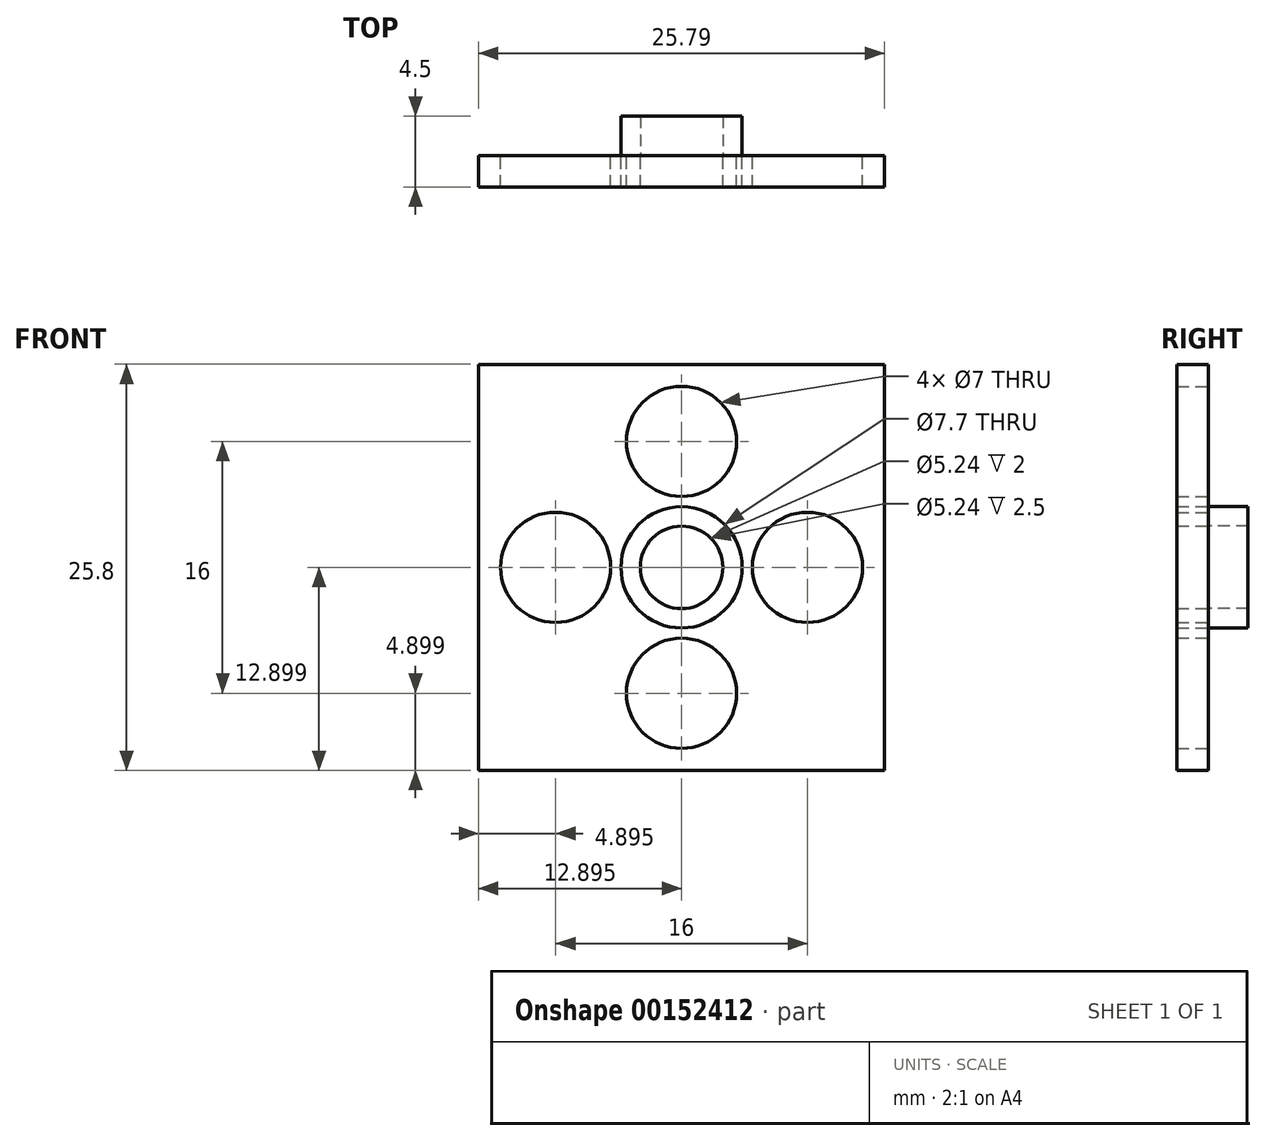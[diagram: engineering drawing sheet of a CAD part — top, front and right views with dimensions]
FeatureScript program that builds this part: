
annotation { "Feature Type Name" : "Feature", "Feature Type Description" : "" }
export const myFeature = defineFeature(function(context is Context, id is Id, definition is map)
    precondition{}
    {
        {
            var Q0;
            Q0=qCreatedBy(makeId("Front.planeOp"),FACE);
            var sketch = newSketch(context, id + "F0", { "sketchPlane" : qUnion([Q0])});
            skPoint(sketch, "E0.middle", {"position": v(0.36, -0.48) * mm});
            skLineSegment(sketch, "E1.top", {"start": v(-7.64, -8.48) * mm, "end": v(8.36, -8.48) * mm, "construction": true});
            skLineSegment(sketch, "E1.left", {"start": v(-7.64, 7.52) * mm, "end": v(-7.64, -8.48) * mm, "construction": true});
            skLineSegment(sketch, "E1.right", {"start": v(8.36, 7.52) * mm, "end": v(8.36, -8.48) * mm, "construction": true});
            skLineSegment(sketch, "E2", {"start": v(-7.64, 7.52) * mm, "end": v(8.36, 7.52) * mm, "construction": true});
            skLineSegment(sketch, "E3", {"start": v(0.36, -0.48) * mm, "end": v(-27.14, 27.02) * mm, "construction": true});
            skLineSegment(sketch, "E4", {"start": v(0.36, -0.48) * mm, "end": v(-27.14, -27.98) * mm, "construction": true});
            skLineSegment(sketch, "E5", {"start": v(0.36, -0.48) * mm, "end": v(27.86, 27.02) * mm, "construction": true});
            skLineSegment(sketch, "E6", {"start": v(0.36, -0.48) * mm, "end": v(27.86, -27.98) * mm, "construction": true});
            skLineSegment(sketch, "E7", {"start": v(0.36, -0.48) * mm, "end": v(0.36, 27.02) * mm, "construction": true});
            skLineSegment(sketch, "E8", {"start": v(0.36, -8.48) * mm, "end": v(0.36, -27.98) * mm, "construction": true});
            skPoint(sketch, "E9", {"position": v(-7.64, 7.52) * mm});
            skLineSegment(sketch, "E10", {"start": v(21.88, 21.04) * mm, "end": v(-21.17, 21.04) * mm, "construction": true});
            skLineSegment(sketch, "E11", {"start": v(-21.17, 21.04) * mm, "end": v(-21.17, -22) * mm, "construction": true});
            skLineSegment(sketch, "E12", {"start": v(-21.17, -22) * mm, "end": v(21.88, -22) * mm, "construction": true});
            skLineSegment(sketch, "E13", {"start": v(21.88, -22) * mm, "end": v(21.88, 21.04) * mm, "construction": true});
            skLineSegment(sketch, "E14", {"start": v(0.36, -0.48) * mm, "end": v(-19.04, -0.48) * mm, "construction": true});
            skLineSegment(sketch, "E15", {"start": v(-27.14, -0.48) * mm, "end": v(-19.04, -0.48) * mm, "construction": true});
            skLineSegment(sketch, "E16", {"start": v(0.36, -0.48) * mm, "end": v(27.86, -0.48) * mm, "construction": true});
            skLineSegment(sketch, "E17", {"start": v(0.36, -0.48) * mm, "end": v(0.36, -8.48) * mm, "construction": true});
            skCircle(sketch, "E18", {"center": v(8.36, -0.48) * mm, "radius": 1.5 * mm});
            skCircle(sketch, "E19", {"center": v(-7.64, -0.48) * mm, "radius": 1.5 * mm});
            skCircle(sketch, "E20", {"center": v(0.36, -8.48) * mm, "radius": 1.5 * mm});
            skLineSegment(sketch, "E21.MirrorCS", {"start": v(0.36, -0.48) * mm, "end": v(19.75, -0.48) * mm, "construction": true});
            skCircle(sketch, "E22", {"center": v(0.36, -0.48) * mm, "radius": 19.53 * mm, "construction": true});
            skLineSegment(sketch, "E23", {"start": v(0.36, 23.08) * mm, "end": v(0.36, 22.48) * mm});
            skCircle(sketch, "E24", {"center": v(0.36, -0.48) * mm, "radius": 2.62 * mm});
            skCircle(sketch, "E25", {"center": v(0.36, -0.48) * mm, "radius": 3.85 * mm});
            skCircle(sketch, "E26", {"center": v(0.36, -0.48) * mm, "radius": 4.9 * mm, "construction": true});
            skCircle(sketch, "E27", {"center": v(8.36, -0.48) * mm, "radius": 3.5 * mm});
            skLineSegment(sketch, "E28.bottom", {"start": v(-12.54, -13.38) * mm, "end": v(13.25, -13.38) * mm});
            skLineSegment(sketch, "E28.top", {"start": v(-12.54, 12.42) * mm, "end": v(13.25, 12.42) * mm});
            skLineSegment(sketch, "E28.left", {"start": v(-12.54, -13.38) * mm, "end": v(-12.54, 12.42) * mm});
            skLineSegment(sketch, "E28.right", {"start": v(13.25, -13.38) * mm, "end": v(13.25, 12.42) * mm});
            skCircle(sketch, "E29.MirrorC", {"center": v(-7.64, -0.48) * mm, "radius": 3.5 * mm});
            skCircle(sketch, "E30.MirrorC", {"center": v(0.36, -8.48) * mm, "radius": 3.5 * mm});
            skCircle(sketch, "E31.MirrorC", {"center": v(0.36, 7.52) * mm, "radius": 3.5 * mm});
            skSolve(sketch);
        }
        {
            var Q0;
            Q0=makeQuery(id+"F0.imprint","IMPRINT",FACE,{"disambiguationData":[TD([[makeQuery(id+"F0.imprint","IMPRINT",EDGE,{"derivedFrom":sQuery(id+"F0.wireOp",EDGE,"E24")}),-1.0]])]});
            extrude(context, id + "F1", {"entities" : qUnion([Q0]), "oppositeDirection" : true, "depth" : 2.5 * mm});
        }
        {
            var Q0;
            Q0=makeQuery(id+"F0.imprint","IMPRINT",FACE,{"disambiguationData":[TD([[makeQuery(id+"F0.imprint","IMPRINT",EDGE,{"derivedFrom":sQuery(id+"F0.wireOp",EDGE,"E25")}),-1.0]])]});
            var Q1;
            Q1=makeQuery(id+"F0.imprint","IMPRINT",FACE,{"disambiguationData":[TD([[makeQuery(id+"F0.imprint","IMPRINT",EDGE,{"derivedFrom":sQuery(id+"F0.wireOp",EDGE,"2a59d5c3-b0ba-4150-aeea-9719cb5647a7")}),-1.0]])]});
            extrude(context, id + "F2", {"entities" : qUnion([Q0, Q1]), "depth" : 2 * mm});
        }
        {
            var Q0;
            Q0=makeQuery(id+"F1.opExtrude","CAP_FACE",FACE,{"disambiguationData":[OSD([sQuery(id+"F0.wireOp",EDGE,"E24"),sQuery(id+"F0.wireOp",EDGE,"E25")])],"isStart":true});
            extrude(context, id + "F3", {"entities" : qUnion([Q0]), "depth" : 2 * mm});
        }
    });
